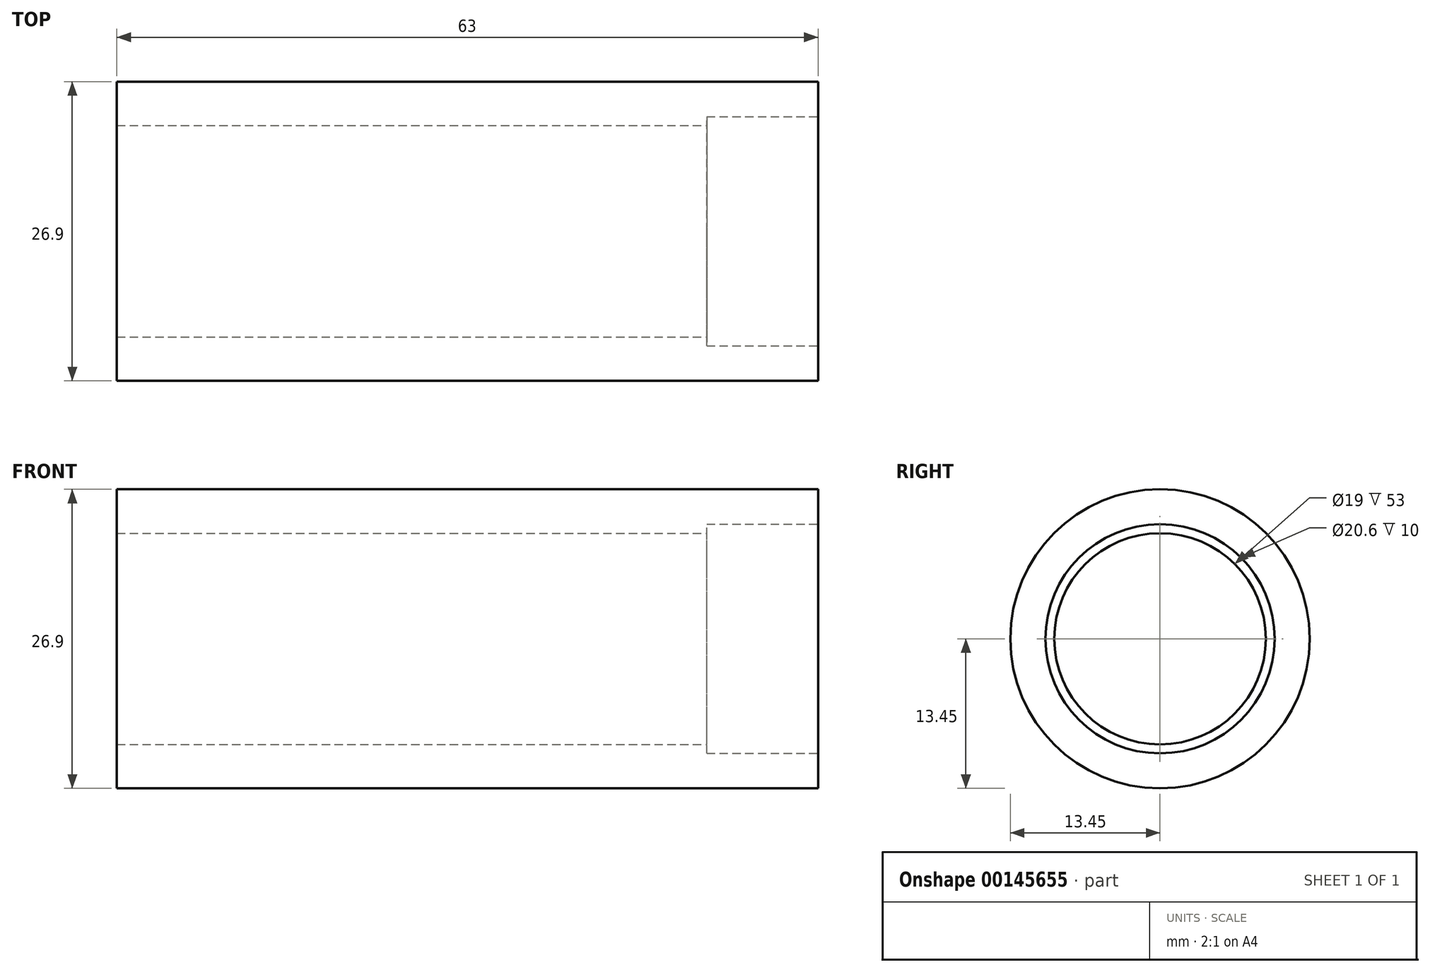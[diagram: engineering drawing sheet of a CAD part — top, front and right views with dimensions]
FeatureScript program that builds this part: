
annotation { "Feature Type Name" : "Feature", "Feature Type Description" : "" }
export const myFeature = defineFeature(function(context is Context, id is Id, definition is map)
    precondition{}
    {
        {
            var Q0;
            Q0=qCreatedBy(makeId("Right.planeOp"),FACE);
            var sketch = newSketch(context, id + "F0", { "sketchPlane" : qUnion([Q0])});
            skCircle(sketch, "E0", {"center": v(0, 0) * mm, "radius": 13.45 * mm});
            skSolve(sketch);
        }
        {
            var Q0;
            Q0=qSketchRegion(id+"F0",true);
            extrude(context, id + "F1", {"entities" : qUnion([Q0]), "depth" : 63 * mm});
        }
        {
            var Q0;
            Q0=makeQuery(id+"F1.opExtrude","CAP_FACE",FACE,{"disambiguationData":[OSD([sQuery(id+"F0.wireOp",EDGE,"E0")])],"isStart":false});
            var sketch = newSketch(context, id + "F2", { "sketchPlane" : qUnion([Q0])});
            skCircle(sketch, "E1", {"center": v(0, 0) * mm, "radius": 9.5 * mm});
            skSolve(sketch);
        }
        {
            var Q0;
            Q0=qSketchRegion(id+"F2",true);
            extrude(context, id + "F3", {"entities" : qUnion([Q0]), "operationType" : NewBodyOperationType.REMOVE, "endBound" : BoundingType.THROUGH_ALL, "oppositeDirection" : true, "depth" : 25 * mm});
        }
        {
            var Q0;
            Q0=makeQuery(id+"F1.opExtrude","CAP_FACE",FACE,{"disambiguationData":[OSD([sQuery(id+"F0.wireOp",EDGE,"E0")])],"isStart":false});
            var sketch = newSketch(context, id + "F4", { "sketchPlane" : qUnion([Q0])});
            skCircle(sketch, "E2", {"center": v(0, 0) * mm, "radius": 10.3 * mm});
            skSolve(sketch);
        }
        {
            var Q0;
            Q0=qSketchRegion(id+"F4",true);
            extrude(context, id + "F5", {"entities" : qUnion([Q0]), "operationType" : NewBodyOperationType.REMOVE, "oppositeDirection" : true, "depth" : 10 * mm});
        }
    });
